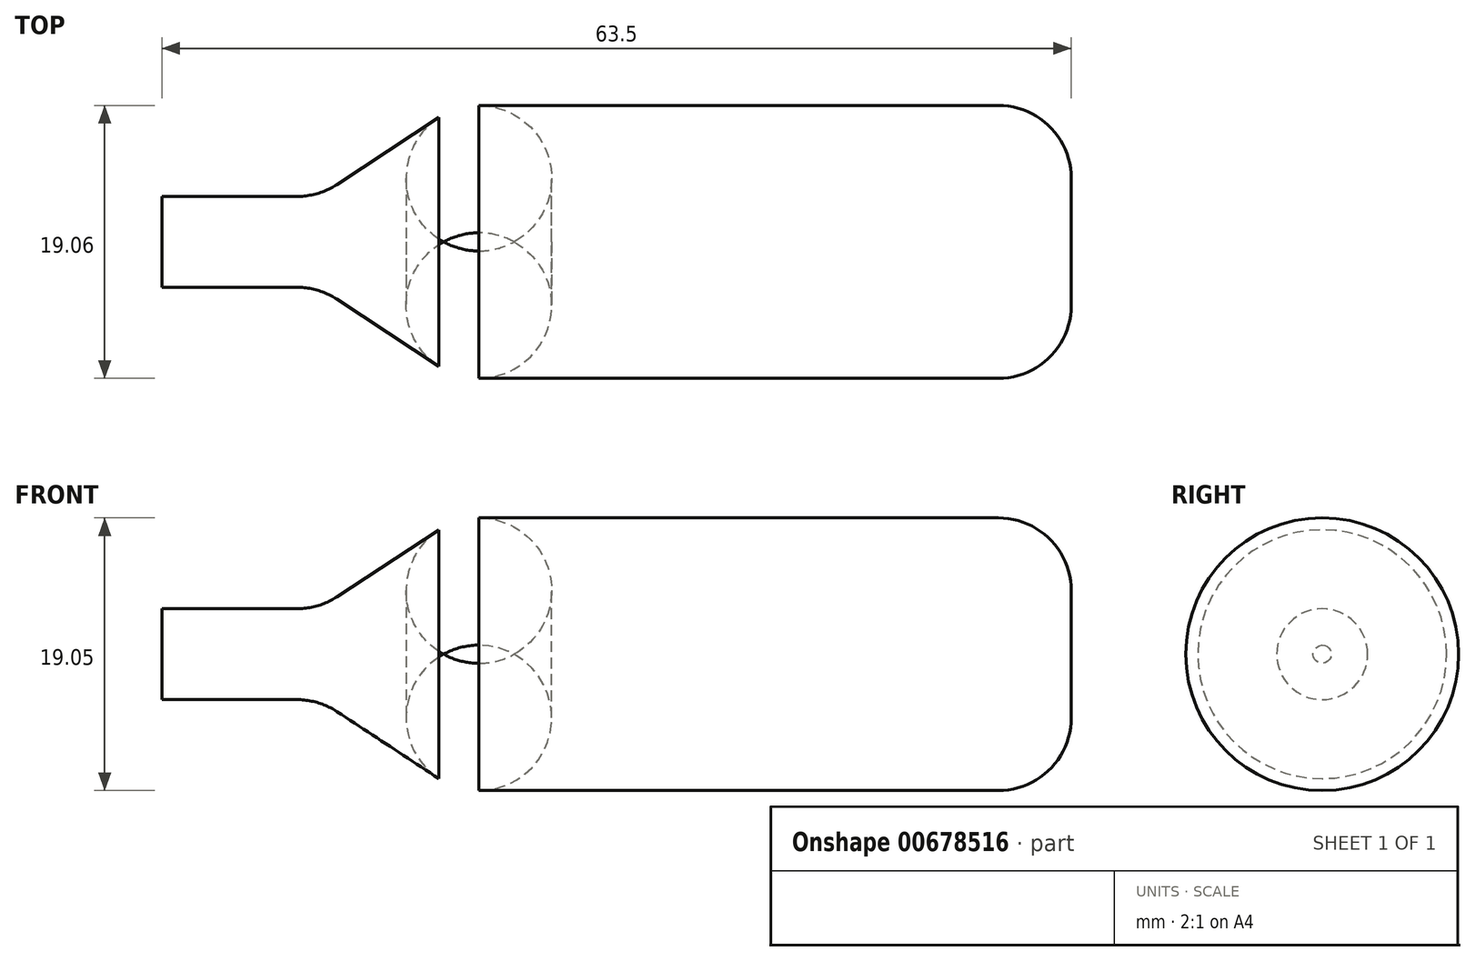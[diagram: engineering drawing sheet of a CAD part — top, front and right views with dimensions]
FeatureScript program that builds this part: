
annotation { "Feature Type Name" : "Feature", "Feature Type Description" : "" }
export const myFeature = defineFeature(function(context is Context, id is Id, definition is map)
    precondition{}
    {
        {
            var Q0;
            Q0=qCreatedBy(makeId("Front.planeOp"),FACE);
            var sketch = newSketch(context, id + "F0", { "sketchPlane" : qUnion([Q0])});
            skLineSegment(sketch, "E0.left", {"start": v(-29.55, -9.42) * mm, "end": v(-29.55, -12.6) * mm});
            skLineSegment(sketch, "E0.right", {"start": v(33.95, -3.07) * mm, "end": v(33.95, -12.6) * mm});
            skLineSegment(sketch, "E1", {"start": v(33.95, -3.07) * mm, "end": v(-8.95, -3.07) * mm});
            skLineSegment(sketch, "E2", {"start": v(-29.55, -9.42) * mm, "end": v(-18.6, -9.42) * mm});
            skLineSegment(sketch, "E3", {"start": v(-18.6, -9.42) * mm, "end": v(-8.95, -3.07) * mm});
            skPoint(sketch, "E4.orphan", {"position": v(-29.55, -4.77) * mm});
            skPoint(sketch, "E5.orphan", {"position": v(-29.55, -3.07) * mm});
            skLineSegment(sketch, "E6", {"start": v(-29.55, -12.6) * mm, "end": v(33.95, -12.6) * mm});
            skSolve(sketch);
        }
        {
            var Q0;
            Q0=makeQuery(id+"F0.imprint","IMPRINT",FACE,{"disambiguationData":[TD([[makeQuery(id+"F0.imprint","IMPRINT",EDGE,{"derivedFrom":sQuery(id+"F0.wireOp",EDGE,"E0.left")}),1.0]])]});
            var Q1;
            Q1=sQuery(id+"F0.wireOp",EDGE,"E6");
            revolve(context, id + "F1", {"entities" : qUnion([Q0]), "axis" : qUnion([Q1]), "revolveType" : RevolveType.FULL});
        }
        {
            var Q0;
            Q0=makeQuery(id+"F1.opRevolve","SWEPT_FACE",FACE,{"disambiguationData":[OSD([sQuery(id+"F0.wireOp",EDGE,"E0.right")])]});
            fillet(context, id + "F2", {"entities" : qUnion([Q0]), "radius" : 5.08 * mm, "tangentPropagation" : true, "allowEdgeOverflow" : false});
        }
        {
            var Q0;
            Q0=makeQuery(id+"F1.opRevolve","SWEPT_FACE",FACE,{"disambiguationData":[OSD([sQuery(id+"F0.wireOp",EDGE,"E3")])]});
            fillet(context, id + "F3", {"entities" : qUnion([Q0]), "radius" : 5.08 * mm, "tangentPropagation" : true, "allowEdgeOverflow" : false});
        }
    });
